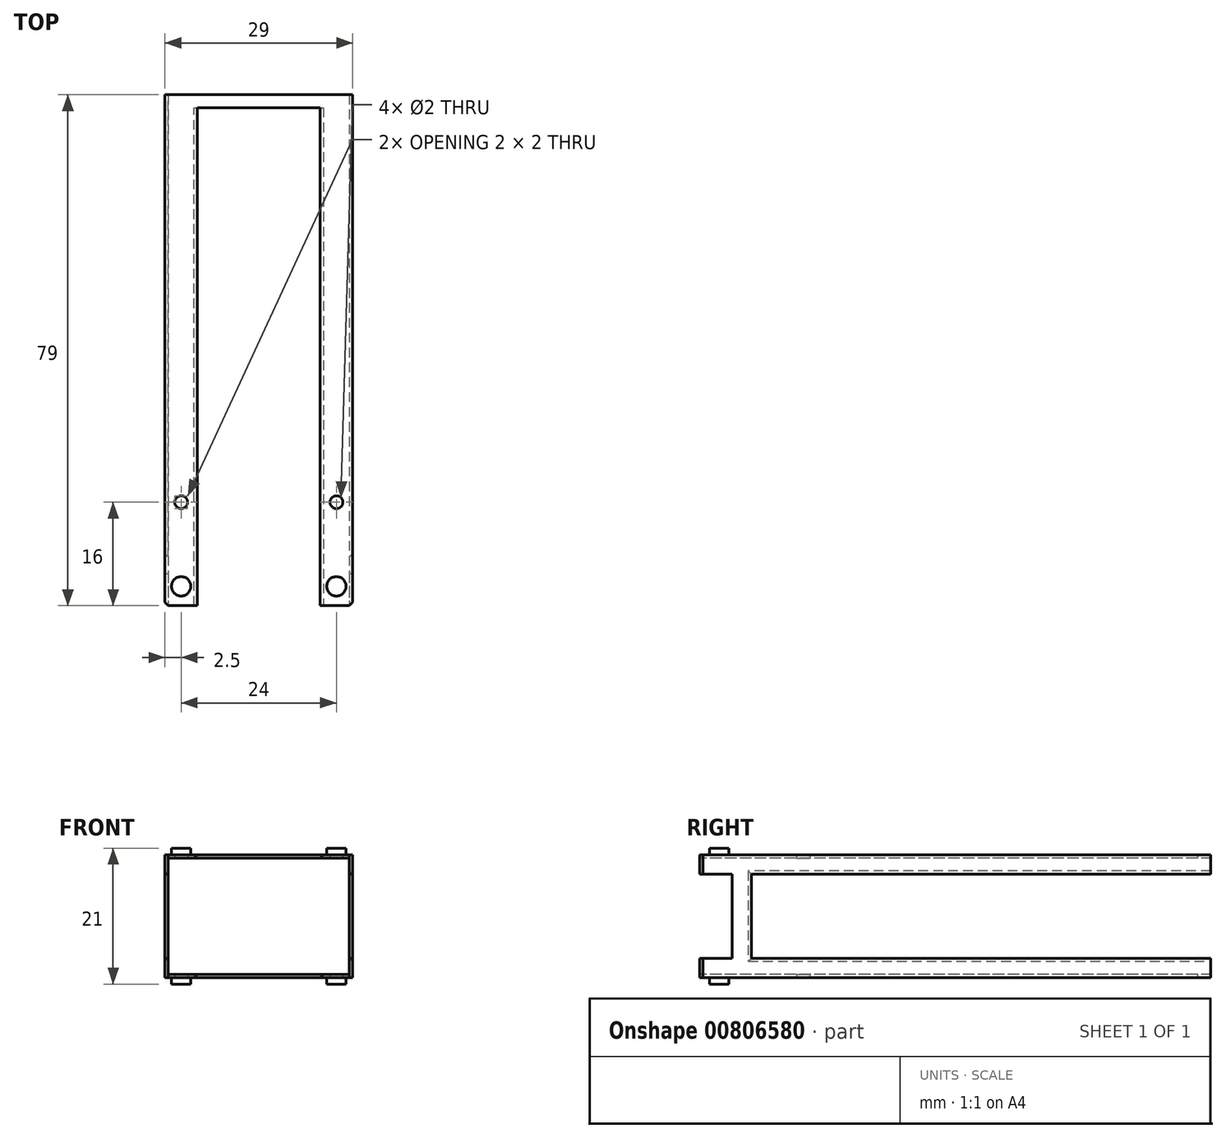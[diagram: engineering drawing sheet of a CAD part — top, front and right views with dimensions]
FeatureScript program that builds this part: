
annotation { "Feature Type Name" : "Feature", "Feature Type Description" : "" }
export const myFeature = defineFeature(function(context is Context, id is Id, definition is map)
    precondition{}
    {
        {
            var Q0;
            Q0=qCreatedBy(makeId("Top.planeOp"),FACE);
            var sketch = newSketch(context, id + "F0", { "sketchPlane" : qUnion([Q0])});
            skLineSegment(sketch, "E0.bottom", {"start": v(-14.5, 79) * mm, "end": v(14.5, 79) * mm});
            skLineSegment(sketch, "E0.top", {"start": v(-14.5, 0) * mm, "end": v(14.5, 0) * mm});
            skLineSegment(sketch, "E0.left", {"start": v(-14.5, 79) * mm, "end": v(-14.5, 0) * mm});
            skLineSegment(sketch, "E0.right", {"start": v(14.5, 79) * mm, "end": v(14.5, 0) * mm});
            skCircle(sketch, "E1", {"center": v(-12, 16) * mm, "radius": 1 * mm});
            skCircle(sketch, "E2", {"center": v(12, 16) * mm, "radius": 1 * mm});
            skCircle(sketch, "E3", {"center": v(-12, 3) * mm, "radius": 1.5 * mm});
            skCircle(sketch, "E4", {"center": v(12, 3) * mm, "radius": 1.5 * mm});
            skSolve(sketch);
        }
        {
            var Q0;
            Q0=makeQuery(id+"F0.imprint","IMPRINT",FACE,{"disambiguationData":[TD([[makeQuery(id+"F0.imprint","IMPRINT",EDGE,{"derivedFrom":sQuery(id+"F0.wireOp",EDGE,"E0.bottom")}),-1.0]])]});
            extrude(context, id + "F1", {"entities" : qUnion([Q0]), "endBound" : BoundingType.SYMMETRIC, "depth" : 19 * mm, "offsetDistance" : 25 * mm});
        }
        {
            var Q0;
            Q0=makeQuery(id+"F0.imprint","IMPRINT",FACE,{"disambiguationData":[TD([[makeQuery(id+"F0.imprint","IMPRINT",EDGE,{"derivedFrom":sQuery(id+"F0.wireOp",EDGE,"E3")}),1.0]])]});
            var Q1;
            Q1=makeQuery(id+"F0.imprint","IMPRINT",FACE,{"disambiguationData":[TD([[makeQuery(id+"F0.imprint","IMPRINT",EDGE,{"derivedFrom":sQuery(id+"F0.wireOp",EDGE,"E4")}),1.0]])]});
            extrude(context, id + "F2", {"entities" : qUnion([Q0, Q1]), "operationType" : NewBodyOperationType.ADD, "endBound" : BoundingType.SYMMETRIC, "depth" : 21 * mm, "offsetDistance" : 25 * mm});
        }
        {
            var Q0;
            Q0=qCreatedBy(makeId("Front.planeOp"),FACE);
            var sketch = newSketch(context, id + "F3", { "sketchPlane" : qUnion([Q0])});
            skLineSegment(sketch, "E5.bottom", {"start": v(-14.5, 9.5) * mm, "end": v(14.5, 9.5) * mm});
            skLineSegment(sketch, "E5.top", {"start": v(-14.5, -9.5) * mm, "end": v(14.5, -9.5) * mm});
            skLineSegment(sketch, "E5.left", {"start": v(-14.5, 9.5) * mm, "end": v(-14.5, -9.5) * mm});
            skLineSegment(sketch, "E5.right", {"start": v(14.5, 9.5) * mm, "end": v(14.5, -9.5) * mm});
            skLineSegment(sketch, "E6.0", {"start": v(-14, 9) * mm, "end": v(14, 9) * mm});
            skLineSegment(sketch, "E6.1", {"start": v(-14, 9) * mm, "end": v(-14, -9) * mm});
            skLineSegment(sketch, "E6.2", {"start": v(-14, -9) * mm, "end": v(14, -9) * mm});
            skLineSegment(sketch, "E6.3", {"start": v(14, 9) * mm, "end": v(14, -9) * mm});
            skLineSegment(sketch, "E7", {"start": v(-14.5, 6.5) * mm, "end": v(-14, 6.5) * mm});
            skLineSegment(sketch, "E8", {"start": v(-14.5, -6.5) * mm, "end": v(-14, -6.5) * mm});
            skLineSegment(sketch, "E9", {"start": v(-9.5, -9) * mm, "end": v(-9.5, -9.5) * mm});
            skLineSegment(sketch, "E10", {"start": v(9.5, -9) * mm, "end": v(9.5, -9.5) * mm});
            skLineSegment(sketch, "E11", {"start": v(14, -6.5) * mm, "end": v(14.5, -6.5) * mm});
            skLineSegment(sketch, "E12", {"start": v(14, 6.5) * mm, "end": v(14.5, 6.5) * mm});
            skLineSegment(sketch, "E13", {"start": v(9.5, 9) * mm, "end": v(9.5, 9.5) * mm});
            skLineSegment(sketch, "E14", {"start": v(-9.5, 9) * mm, "end": v(-9.5, 9.5) * mm});
            skSolve(sketch);
        }
        {
            var Q0;
            {var subQ1=sQuery(id+"F3.wireOp",EDGE,"E6.0");var subQ8=sQuery(id+"F3.wireOp",EDGE,"E6.1");var subQ12=makeQuery(id+"F3.imprint","INTERSECT",VERTEX,{"derivedFrom":[subQ1,subQ8]});Q0=makeQuery(id+"F3.imprint","IMPRINT",FACE,{"disambiguationData":[TD([[makeQuery(id+"F3.imprint","IMPRINT",EDGE,{"disambiguationData":[TD([[subQ12,-1.0]])],"derivedFrom":subQ1}),-1.0]])]});}
            var Q1;
            {var subQ0=sQuery(id+"F3.wireOp",EDGE,"E7");Q1=makeQuery(id+"F3.imprint","IMPRINT",FACE,{"disambiguationData":[TD([[makeQuery(id+"F3.imprint","IMPRINT",EDGE,{"derivedFrom":subQ0}),-1.0]])]});}
            var Q2;
            {var subQ0=sQuery(id+"F3.wireOp",EDGE,"E13");Q2=makeQuery(id+"F3.imprint","IMPRINT",FACE,{"disambiguationData":[TD([[makeQuery(id+"F3.imprint","IMPRINT",EDGE,{"derivedFrom":subQ0}),1.0]])]});}
            var Q3;
            {var subQ0=sQuery(id+"F3.wireOp",EDGE,"E11");Q3=makeQuery(id+"F3.imprint","IMPRINT",FACE,{"disambiguationData":[TD([[makeQuery(id+"F3.imprint","IMPRINT",EDGE,{"derivedFrom":subQ0}),1.0]])]});}
            var Q4;
            {var subQ0=sQuery(id+"F3.wireOp",EDGE,"E9");Q4=makeQuery(id+"F3.imprint","IMPRINT",FACE,{"disambiguationData":[TD([[makeQuery(id+"F3.imprint","IMPRINT",EDGE,{"derivedFrom":subQ0}),1.0]])]});}
            extrude(context, id + "F4", {"entities" : qUnion([Q0, Q1, Q2, Q3, Q4]), "operationType" : NewBodyOperationType.REMOVE, "oppositeDirection" : true, "depth" : 77 * mm, "offsetDistance" : 25 * mm});
        }
        {
            var Q0;
            {var subQ1=sQuery(id+"F3.wireOp",EDGE,"E6.0");var subQ8=sQuery(id+"F3.wireOp",EDGE,"E6.1");var subQ12=makeQuery(id+"F3.imprint","INTERSECT",VERTEX,{"derivedFrom":[subQ1,subQ8]});Q0=makeQuery(id+"F3.imprint","IMPRINT",FACE,{"disambiguationData":[TD([[makeQuery(id+"F3.imprint","IMPRINT",EDGE,{"disambiguationData":[TD([[subQ12,-1.0]])],"derivedFrom":subQ1}),-1.0]])]});}
            var Q1;
            {var subQ0=sQuery(id+"F3.wireOp",EDGE,"E7");Q1=makeQuery(id+"F3.imprint","IMPRINT",FACE,{"disambiguationData":[TD([[makeQuery(id+"F3.imprint","IMPRINT",EDGE,{"derivedFrom":subQ0}),-1.0]])]});}
            var Q2;
            {var subQ0=sQuery(id+"F3.wireOp",EDGE,"E11");Q2=makeQuery(id+"F3.imprint","IMPRINT",FACE,{"disambiguationData":[TD([[makeQuery(id+"F3.imprint","IMPRINT",EDGE,{"derivedFrom":subQ0}),1.0]])]});}
            extrude(context, id + "F5", {"entities" : qUnion([Q0, Q1, Q2]), "operationType" : NewBodyOperationType.REMOVE, "oppositeDirection" : true, "depth" : 79 * mm, "offsetDistance" : 25 * mm});
        }
        {
            var Q0;
            {var subQ0=sQuery(id+"F3.wireOp",EDGE,"E7");Q0=makeQuery(id+"F3.imprint","IMPRINT",FACE,{"disambiguationData":[TD([[makeQuery(id+"F3.imprint","IMPRINT",EDGE,{"derivedFrom":subQ0}),-1.0]])]});}
            var Q1;
            {var subQ0=sQuery(id+"F3.wireOp",EDGE,"E11");Q1=makeQuery(id+"F3.imprint","IMPRINT",FACE,{"disambiguationData":[TD([[makeQuery(id+"F3.imprint","IMPRINT",EDGE,{"derivedFrom":subQ0}),1.0]])]});}
            extrude(context, id + "F6", {"entities" : qUnion([Q0, Q1]), "operationType" : NewBodyOperationType.ADD, "oppositeDirection" : true, "depth" : 8 * mm, "offsetDistance" : 25 * mm});
        }
        {
            var Q0;
            {var subQ0=sQuery(id+"F3.wireOp",EDGE,"E7");Q0=makeQuery(id+"F3.imprint","IMPRINT",FACE,{"disambiguationData":[TD([[makeQuery(id+"F3.imprint","IMPRINT",EDGE,{"derivedFrom":subQ0}),-1.0]])]});}
            var Q1;
            {var subQ0=sQuery(id+"F3.wireOp",EDGE,"E11");Q1=makeQuery(id+"F3.imprint","IMPRINT",FACE,{"disambiguationData":[TD([[makeQuery(id+"F3.imprint","IMPRINT",EDGE,{"derivedFrom":subQ0}),1.0]])]});}
            extrude(context, id + "F7", {"entities" : qUnion([Q0, Q1]), "operationType" : NewBodyOperationType.REMOVE, "oppositeDirection" : true, "depth" : 5 * mm, "offsetDistance" : 25 * mm});
        }
        {
            var Q0;
            Q0=makeQuery(id+"F4.boolean.opBoolean","COPY",EDGE,{"derivedFrom":makeQuery(id+"F4.opExtrude","SWEPT_EDGE",EDGE,{"disambiguationData":[OSD([sQuery(id+"F3.wireOp",EDGE,"E6.2"),sQuery(id+"F3.wireOp",EDGE,"E9")])]})});
            var Q1;
            Q1=makeQuery(id+"F4.boolean.opBoolean","COPY",EDGE,{"derivedFrom":makeQuery(id+"F4.opExtrude","SWEPT_EDGE",EDGE,{"disambiguationData":[OSD([sQuery(id+"F3.wireOp",EDGE,"E6.2"),sQuery(id+"F3.wireOp",EDGE,"E10")])]})});
            var Q2;
            Q2=makeQuery(id+"F4.boolean.opBoolean","COPY",EDGE,{"derivedFrom":makeQuery(id+"F4.opExtrude","SWEPT_EDGE",EDGE,{"disambiguationData":[OSD([sQuery(id+"F3.wireOp",EDGE,"E6.3"),sQuery(id+"F3.wireOp",EDGE,"E11")])]})});
            var Q3;
            Q3=makeQuery(id+"F4.boolean.opBoolean","COPY",EDGE,{"derivedFrom":makeQuery(id+"F4.opExtrude","SWEPT_EDGE",EDGE,{"disambiguationData":[OSD([sQuery(id+"F3.wireOp",EDGE,"E6.1"),sQuery(id+"F3.wireOp",EDGE,"E8")])]})});
            var Q4;
            Q4=makeQuery(id+"F4.boolean.opBoolean","COPY",EDGE,{"derivedFrom":makeQuery(id+"F4.opExtrude","SWEPT_EDGE",EDGE,{"disambiguationData":[OSD([sQuery(id+"F3.wireOp",EDGE,"E6.3"),sQuery(id+"F3.wireOp",EDGE,"E12")])]})});
            var Q5;
            Q5=makeQuery(id+"F4.boolean.opBoolean","COPY",EDGE,{"derivedFrom":makeQuery(id+"F4.opExtrude","SWEPT_EDGE",EDGE,{"disambiguationData":[OSD([sQuery(id+"F3.wireOp",EDGE,"E6.0"),sQuery(id+"F3.wireOp",EDGE,"E13")])]})});
            var Q6;
            Q6=makeQuery(id+"F4.boolean.opBoolean","COPY",EDGE,{"derivedFrom":makeQuery(id+"F4.opExtrude","SWEPT_EDGE",EDGE,{"disambiguationData":[OSD([sQuery(id+"F3.wireOp",EDGE,"E6.1"),sQuery(id+"F3.wireOp",EDGE,"E7")])]})});
            var Q7;
            Q7=makeQuery(id+"F4.boolean.opBoolean","COPY",EDGE,{"derivedFrom":makeQuery(id+"F4.opExtrude","SWEPT_EDGE",EDGE,{"disambiguationData":[OSD([sQuery(id+"F3.wireOp",EDGE,"E6.0"),sQuery(id+"F3.wireOp",EDGE,"E14")])]})});
            var Q8;
            {var subQ0=sQuery(id+"F3.wireOp",EDGE,"E6.3");Q8=makeQuery(id+"F5.boolean.opBoolean","INTERSECT",EDGE,{"derivedFrom":[makeQuery(id+"F4.boolean.opBoolean","COPY",FACE,{"derivedFrom":makeQuery(id+"F4.opExtrude","CAP_FACE",FACE,{"disambiguationData":[OSD([sQuery(id+"F3.wireOp",EDGE,"E5.bottom"),sQuery(id+"F3.wireOp",EDGE,"E5.top"),sQuery(id+"F3.wireOp",EDGE,"E5.left"),sQuery(id+"F3.wireOp",EDGE,"E5.right"),sQuery(id+"F3.wireOp",EDGE,"E6.0"),sQuery(id+"F3.wireOp",EDGE,"E6.1"),sQuery(id+"F3.wireOp",EDGE,"E6.2"),subQ0,sQuery(id+"F3.wireOp",EDGE,"E7"),sQuery(id+"F3.wireOp",EDGE,"E8"),sQuery(id+"F3.wireOp",EDGE,"E9"),sQuery(id+"F3.wireOp",EDGE,"E10"),sQuery(id+"F3.wireOp",EDGE,"E11"),sQuery(id+"F3.wireOp",EDGE,"E12"),sQuery(id+"F3.wireOp",EDGE,"E13"),sQuery(id+"F3.wireOp",EDGE,"E14")])],"isStart":false})}),makeQuery(id+"F5.opExtrude","SWEPT_FACE",FACE,{"disambiguationData":[OSD([subQ0])]})]});}
            var Q9;
            {var subQ0=sQuery(id+"F3.wireOp",EDGE,"E6.1");Q9=makeQuery(id+"F5.boolean.opBoolean","INTERSECT",EDGE,{"derivedFrom":[makeQuery(id+"F4.boolean.opBoolean","COPY",FACE,{"derivedFrom":makeQuery(id+"F4.opExtrude","CAP_FACE",FACE,{"disambiguationData":[OSD([sQuery(id+"F3.wireOp",EDGE,"E5.bottom"),sQuery(id+"F3.wireOp",EDGE,"E5.top"),sQuery(id+"F3.wireOp",EDGE,"E5.left"),sQuery(id+"F3.wireOp",EDGE,"E5.right"),sQuery(id+"F3.wireOp",EDGE,"E6.0"),subQ0,sQuery(id+"F3.wireOp",EDGE,"E6.2"),sQuery(id+"F3.wireOp",EDGE,"E6.3"),sQuery(id+"F3.wireOp",EDGE,"E7"),sQuery(id+"F3.wireOp",EDGE,"E8"),sQuery(id+"F3.wireOp",EDGE,"E9"),sQuery(id+"F3.wireOp",EDGE,"E10"),sQuery(id+"F3.wireOp",EDGE,"E11"),sQuery(id+"F3.wireOp",EDGE,"E12"),sQuery(id+"F3.wireOp",EDGE,"E13"),sQuery(id+"F3.wireOp",EDGE,"E14")])],"isStart":false})}),makeQuery(id+"F5.opExtrude","SWEPT_FACE",FACE,{"disambiguationData":[OSD([subQ0])]})]});}
            var Q10;
            Q10=makeQuery(id+"F7.boolean.opBoolean","COPY",EDGE,{"derivedFrom":makeQuery(id+"F7.opExtrude","CAP_EDGE",EDGE,{"disambiguationData":[OSD([sQuery(id+"F3.wireOp",EDGE,"E6.0")])],"isStart":false})});
            var Q11;
            {var subQ0=sQuery(id+"F0.wireOp",EDGE,"E0.right");var subQ1=makeQuery(id+"F1.opExtrude","SWEPT_FACE",FACE,{"disambiguationData":[OSD([subQ0])]});var subQ3=sQuery(id+"F0.wireOp",EDGE,"E0.top");var subQ6=sQuery(id+"F3.wireOp",EDGE,"E5.bottom");var subQ7=sQuery(id+"F0.wireOp",EDGE,"E0.left");var subQ10=makeQuery(id+"F1.opExtrude","CAP_EDGE",EDGE,{"disambiguationData":[OSD([subQ3])],"isStart":false});Q11=makeQuery(id+"F7.boolean.opBoolean","SPLIT",EDGE,{"disambiguationData":[TD([subQ1])],"derivedFrom":makeQuery(id+"F6.boolean.opBoolean","MERGE",EDGE,{"derivedFrom":[makeQuery(id+"F4.boolean.opBoolean","SPLIT",EDGE,{"disambiguationData":[TD([makeQuery(id+"F1.opExtrude","SWEPT_FACE",FACE,{"disambiguationData":[OSD([subQ7])]})])],"derivedFrom":subQ10}),makeQuery(id+"F4.boolean.opBoolean","SPLIT",EDGE,{"disambiguationData":[TD([subQ1])],"derivedFrom":subQ10}),makeQuery(id+"F6.opExtrude","CAP_EDGE",EDGE,{"disambiguationData":[OSD([subQ6])],"isStart":true})]})});}
            var Q12;
            {var subQ0=sQuery(id+"F0.wireOp",EDGE,"E0.right");var subQ2=sQuery(id+"F3.wireOp",EDGE,"E12");var subQ3=sQuery(id+"F3.wireOp",EDGE,"E11");var subQ4=sQuery(id+"F3.wireOp",EDGE,"E5.right");var subQ5=sQuery(id+"F0.wireOp",EDGE,"E0.top");var subQ12=sQuery(id+"F3.wireOp",EDGE,"E5.top");var subQ13=makeQuery(id+"F1.opExtrude","SWEPT_EDGE",EDGE,{"disambiguationData":[OSD([subQ5,subQ0])]});Q12=makeQuery(id+"F7.boolean.opBoolean","SPLIT",EDGE,{"disambiguationData":[TD([makeQuery(id+"F6.opExtrude","SWEPT_FACE",FACE,{"disambiguationData":[OSD([subQ12])]})])],"derivedFrom":makeQuery(id+"F6.boolean.opBoolean","MERGE",EDGE,{"derivedFrom":[makeQuery(id+"F4.boolean.opBoolean","SPLIT",EDGE,{"disambiguationData":[TD([makeQuery(id+"F4.opExtrude","SWEPT_FACE",FACE,{"disambiguationData":[OSD([subQ3])]})])],"derivedFrom":subQ13}),makeQuery(id+"F4.boolean.opBoolean","SPLIT",EDGE,{"disambiguationData":[TD([makeQuery(id+"F4.opExtrude","SWEPT_FACE",FACE,{"disambiguationData":[OSD([subQ2])]})])],"derivedFrom":subQ13}),makeQuery(id+"F6.opExtrude","CAP_EDGE",EDGE,{"disambiguationData":[OSD([subQ4])],"isStart":true})]})});}
            var Q13;
            {var subQ0=sQuery(id+"F0.wireOp",EDGE,"E0.right");var subQ2=sQuery(id+"F3.wireOp",EDGE,"E12");var subQ3=sQuery(id+"F3.wireOp",EDGE,"E11");var subQ4=sQuery(id+"F3.wireOp",EDGE,"E5.right");var subQ5=sQuery(id+"F0.wireOp",EDGE,"E0.top");var subQ7=sQuery(id+"F3.wireOp",EDGE,"E5.bottom");var subQ13=makeQuery(id+"F1.opExtrude","SWEPT_EDGE",EDGE,{"disambiguationData":[OSD([subQ5,subQ0])]});Q13=makeQuery(id+"F7.boolean.opBoolean","SPLIT",EDGE,{"disambiguationData":[TD([makeQuery(id+"F6.opExtrude","SWEPT_FACE",FACE,{"disambiguationData":[OSD([subQ7])]})])],"derivedFrom":makeQuery(id+"F6.boolean.opBoolean","MERGE",EDGE,{"derivedFrom":[makeQuery(id+"F4.boolean.opBoolean","SPLIT",EDGE,{"disambiguationData":[TD([makeQuery(id+"F4.opExtrude","SWEPT_FACE",FACE,{"disambiguationData":[OSD([subQ3])]})])],"derivedFrom":subQ13}),makeQuery(id+"F4.boolean.opBoolean","SPLIT",EDGE,{"disambiguationData":[TD([makeQuery(id+"F4.opExtrude","SWEPT_FACE",FACE,{"disambiguationData":[OSD([subQ2])]})])],"derivedFrom":subQ13}),makeQuery(id+"F6.opExtrude","CAP_EDGE",EDGE,{"disambiguationData":[OSD([subQ4])],"isStart":true})]})});}
            var Q14;
            {var subQ0=sQuery(id+"F0.wireOp",EDGE,"E0.right");var subQ1=makeQuery(id+"F1.opExtrude","SWEPT_FACE",FACE,{"disambiguationData":[OSD([subQ0])]});var subQ3=sQuery(id+"F0.wireOp",EDGE,"E0.top");var subQ5=sQuery(id+"F0.wireOp",EDGE,"E0.left");var subQ7=sQuery(id+"F3.wireOp",EDGE,"E5.top");var subQ10=makeQuery(id+"F1.opExtrude","CAP_EDGE",EDGE,{"disambiguationData":[OSD([subQ3])],"isStart":true});Q14=makeQuery(id+"F7.boolean.opBoolean","SPLIT",EDGE,{"disambiguationData":[TD([subQ1])],"derivedFrom":makeQuery(id+"F6.boolean.opBoolean","MERGE",EDGE,{"derivedFrom":[makeQuery(id+"F4.boolean.opBoolean","SPLIT",EDGE,{"disambiguationData":[TD([makeQuery(id+"F1.opExtrude","SWEPT_FACE",FACE,{"disambiguationData":[OSD([subQ5])]})])],"derivedFrom":subQ10}),makeQuery(id+"F4.boolean.opBoolean","SPLIT",EDGE,{"disambiguationData":[TD([subQ1])],"derivedFrom":subQ10}),makeQuery(id+"F6.opExtrude","CAP_EDGE",EDGE,{"disambiguationData":[OSD([subQ7])],"isStart":true})]})});}
            var Q15;
            {var subQ0=sQuery(id+"F0.wireOp",EDGE,"E0.left");var subQ1=makeQuery(id+"F1.opExtrude","SWEPT_FACE",FACE,{"disambiguationData":[OSD([subQ0])]});var subQ2=sQuery(id+"F0.wireOp",EDGE,"E0.top");var subQ4=sQuery(id+"F0.wireOp",EDGE,"E0.right");var subQ7=sQuery(id+"F3.wireOp",EDGE,"E5.top");var subQ10=makeQuery(id+"F1.opExtrude","CAP_EDGE",EDGE,{"disambiguationData":[OSD([subQ2])],"isStart":true});Q15=makeQuery(id+"F7.boolean.opBoolean","SPLIT",EDGE,{"disambiguationData":[TD([subQ1])],"derivedFrom":makeQuery(id+"F6.boolean.opBoolean","MERGE",EDGE,{"derivedFrom":[makeQuery(id+"F4.boolean.opBoolean","SPLIT",EDGE,{"disambiguationData":[TD([subQ1])],"derivedFrom":subQ10}),makeQuery(id+"F4.boolean.opBoolean","SPLIT",EDGE,{"disambiguationData":[TD([makeQuery(id+"F1.opExtrude","SWEPT_FACE",FACE,{"disambiguationData":[OSD([subQ4])]})])],"derivedFrom":subQ10}),makeQuery(id+"F6.opExtrude","CAP_EDGE",EDGE,{"disambiguationData":[OSD([subQ7])],"isStart":true})]})});}
            var Q16;
            Q16=makeQuery(id+"F7.boolean.opBoolean","COPY",EDGE,{"derivedFrom":makeQuery(id+"F7.opExtrude","CAP_EDGE",EDGE,{"disambiguationData":[OSD([sQuery(id+"F3.wireOp",EDGE,"E6.2")])],"isStart":false})});
            var Q17;
            {var subQ0=sQuery(id+"F0.wireOp",EDGE,"E0.left");var subQ2=sQuery(id+"F0.wireOp",EDGE,"E0.top");var subQ9=sQuery(id+"F3.wireOp",EDGE,"E5.left");var subQ10=sQuery(id+"F3.wireOp",EDGE,"E5.top");var subQ11=sQuery(id+"F3.wireOp",EDGE,"E8");var subQ12=sQuery(id+"F3.wireOp",EDGE,"E7");var subQ13=makeQuery(id+"F1.opExtrude","SWEPT_EDGE",EDGE,{"disambiguationData":[OSD([subQ2,subQ0])]});Q17=makeQuery(id+"F7.boolean.opBoolean","SPLIT",EDGE,{"disambiguationData":[TD([makeQuery(id+"F6.opExtrude","SWEPT_FACE",FACE,{"disambiguationData":[OSD([subQ10])]})])],"derivedFrom":makeQuery(id+"F6.boolean.opBoolean","MERGE",EDGE,{"derivedFrom":[makeQuery(id+"F4.boolean.opBoolean","SPLIT",EDGE,{"disambiguationData":[TD([makeQuery(id+"F4.opExtrude","SWEPT_FACE",FACE,{"disambiguationData":[OSD([subQ11])]})])],"derivedFrom":subQ13}),makeQuery(id+"F4.boolean.opBoolean","SPLIT",EDGE,{"disambiguationData":[TD([makeQuery(id+"F4.opExtrude","SWEPT_FACE",FACE,{"disambiguationData":[OSD([subQ12])]})])],"derivedFrom":subQ13}),makeQuery(id+"F6.opExtrude","CAP_EDGE",EDGE,{"disambiguationData":[OSD([subQ9])],"isStart":true})]})});}
            var Q18;
            {var subQ0=sQuery(id+"F0.wireOp",EDGE,"E0.left");var subQ2=sQuery(id+"F0.wireOp",EDGE,"E0.top");var subQ4=sQuery(id+"F3.wireOp",EDGE,"E5.bottom");var subQ10=sQuery(id+"F3.wireOp",EDGE,"E8");var subQ11=sQuery(id+"F3.wireOp",EDGE,"E7");var subQ12=sQuery(id+"F3.wireOp",EDGE,"E5.left");var subQ13=makeQuery(id+"F1.opExtrude","SWEPT_EDGE",EDGE,{"disambiguationData":[OSD([subQ2,subQ0])]});Q18=makeQuery(id+"F7.boolean.opBoolean","SPLIT",EDGE,{"disambiguationData":[TD([makeQuery(id+"F6.opExtrude","SWEPT_FACE",FACE,{"disambiguationData":[OSD([subQ4])]})])],"derivedFrom":makeQuery(id+"F6.boolean.opBoolean","MERGE",EDGE,{"derivedFrom":[makeQuery(id+"F4.boolean.opBoolean","SPLIT",EDGE,{"disambiguationData":[TD([makeQuery(id+"F4.opExtrude","SWEPT_FACE",FACE,{"disambiguationData":[OSD([subQ10])]})])],"derivedFrom":subQ13}),makeQuery(id+"F4.boolean.opBoolean","SPLIT",EDGE,{"disambiguationData":[TD([makeQuery(id+"F4.opExtrude","SWEPT_FACE",FACE,{"disambiguationData":[OSD([subQ11])]})])],"derivedFrom":subQ13}),makeQuery(id+"F6.opExtrude","CAP_EDGE",EDGE,{"disambiguationData":[OSD([subQ12])],"isStart":true})]})});}
            var Q19;
            {var subQ0=sQuery(id+"F0.wireOp",EDGE,"E0.left");var subQ1=makeQuery(id+"F1.opExtrude","SWEPT_FACE",FACE,{"disambiguationData":[OSD([subQ0])]});var subQ3=sQuery(id+"F0.wireOp",EDGE,"E0.top");var subQ5=sQuery(id+"F3.wireOp",EDGE,"E5.bottom");var subQ6=sQuery(id+"F0.wireOp",EDGE,"E0.right");var subQ10=makeQuery(id+"F1.opExtrude","CAP_EDGE",EDGE,{"disambiguationData":[OSD([subQ3])],"isStart":false});Q19=makeQuery(id+"F7.boolean.opBoolean","SPLIT",EDGE,{"disambiguationData":[TD([subQ1])],"derivedFrom":makeQuery(id+"F6.boolean.opBoolean","MERGE",EDGE,{"derivedFrom":[makeQuery(id+"F4.boolean.opBoolean","SPLIT",EDGE,{"disambiguationData":[TD([subQ1])],"derivedFrom":subQ10}),makeQuery(id+"F4.boolean.opBoolean","SPLIT",EDGE,{"disambiguationData":[TD([makeQuery(id+"F1.opExtrude","SWEPT_FACE",FACE,{"disambiguationData":[OSD([subQ6])]})])],"derivedFrom":subQ10}),makeQuery(id+"F6.opExtrude","CAP_EDGE",EDGE,{"disambiguationData":[OSD([subQ5])],"isStart":true})]})});}
            var Q20;
            Q20=makeQuery(id+"F7.boolean.opBoolean","COPY",EDGE,{"derivedFrom":makeQuery(id+"F7.opExtrude","CAP_EDGE",EDGE,{"disambiguationData":[OSD([sQuery(id+"F3.wireOp",EDGE,"E6.1")])],"isStart":false})});
            var Q21;
            Q21=makeQuery(id+"F7.boolean.opBoolean","COPY",EDGE,{"derivedFrom":makeQuery(id+"F7.opExtrude","CAP_EDGE",EDGE,{"disambiguationData":[OSD([sQuery(id+"F3.wireOp",EDGE,"E6.3")])],"isStart":false})});
            var Q22;
            Q22=makeQuery(id+"F6.opExtrude","CAP_EDGE",EDGE,{"disambiguationData":[OSD([sQuery(id+"F3.wireOp",EDGE,"E6.1")])],"isStart":false});
            var Q23;
            Q23=makeQuery(id+"F6.opExtrude","CAP_EDGE",EDGE,{"disambiguationData":[OSD([sQuery(id+"F3.wireOp",EDGE,"E6.3")])],"isStart":false});
            var Q24;
            {var subQ0=sQuery(id+"F3.wireOp",EDGE,"E5.left");var subQ1=sQuery(id+"F0.wireOp",EDGE,"E0.left");var subQ3=sQuery(id+"F0.wireOp",EDGE,"E0.top");var subQ12=sQuery(id+"F3.wireOp",EDGE,"E8");var subQ13=sQuery(id+"F3.wireOp",EDGE,"E7");var subQ14=makeQuery(id+"F1.opExtrude","SWEPT_EDGE",EDGE,{"disambiguationData":[OSD([subQ3,subQ1])]});Q24=makeQuery(id+"F7.boolean.opBoolean","SPLIT",EDGE,{"disambiguationData":[TD([makeQuery(id+"F7.opExtrude","SWEPT_FACE",FACE,{"disambiguationData":[OSD([subQ12])]})])],"derivedFrom":makeQuery(id+"F6.boolean.opBoolean","MERGE",EDGE,{"derivedFrom":[makeQuery(id+"F4.boolean.opBoolean","SPLIT",EDGE,{"disambiguationData":[TD([makeQuery(id+"F4.opExtrude","SWEPT_FACE",FACE,{"disambiguationData":[OSD([subQ12])]})])],"derivedFrom":subQ14}),makeQuery(id+"F4.boolean.opBoolean","SPLIT",EDGE,{"disambiguationData":[TD([makeQuery(id+"F4.opExtrude","SWEPT_FACE",FACE,{"disambiguationData":[OSD([subQ13])]})])],"derivedFrom":subQ14}),makeQuery(id+"F6.opExtrude","CAP_EDGE",EDGE,{"disambiguationData":[OSD([subQ0])],"isStart":true})]})});}
            var Q25;
            {var subQ0=sQuery(id+"F3.wireOp",EDGE,"E5.right");var subQ1=sQuery(id+"F0.wireOp",EDGE,"E0.right");var subQ3=sQuery(id+"F0.wireOp",EDGE,"E0.top");var subQ12=sQuery(id+"F3.wireOp",EDGE,"E12");var subQ13=sQuery(id+"F3.wireOp",EDGE,"E11");var subQ14=makeQuery(id+"F1.opExtrude","SWEPT_EDGE",EDGE,{"disambiguationData":[OSD([subQ3,subQ1])]});Q25=makeQuery(id+"F7.boolean.opBoolean","SPLIT",EDGE,{"disambiguationData":[TD([makeQuery(id+"F7.opExtrude","SWEPT_FACE",FACE,{"disambiguationData":[OSD([subQ13])]})])],"derivedFrom":makeQuery(id+"F6.boolean.opBoolean","MERGE",EDGE,{"derivedFrom":[makeQuery(id+"F4.boolean.opBoolean","SPLIT",EDGE,{"disambiguationData":[TD([makeQuery(id+"F4.opExtrude","SWEPT_FACE",FACE,{"disambiguationData":[OSD([subQ13])]})])],"derivedFrom":subQ14}),makeQuery(id+"F4.boolean.opBoolean","SPLIT",EDGE,{"disambiguationData":[TD([makeQuery(id+"F4.opExtrude","SWEPT_FACE",FACE,{"disambiguationData":[OSD([subQ12])]})])],"derivedFrom":subQ14}),makeQuery(id+"F6.opExtrude","CAP_EDGE",EDGE,{"disambiguationData":[OSD([subQ0])],"isStart":true})]})});}
            var Q26;
            {var subQ0=sQuery(id+"F3.wireOp",EDGE,"E5.right");var subQ1=sQuery(id+"F0.wireOp",EDGE,"E0.right");var subQ3=sQuery(id+"F0.wireOp",EDGE,"E0.top");var subQ5=sQuery(id+"F3.wireOp",EDGE,"E12");var subQ13=sQuery(id+"F3.wireOp",EDGE,"E11");var subQ14=makeQuery(id+"F1.opExtrude","SWEPT_EDGE",EDGE,{"disambiguationData":[OSD([subQ3,subQ1])]});Q26=makeQuery(id+"F7.boolean.opBoolean","SPLIT",EDGE,{"disambiguationData":[TD([makeQuery(id+"F7.opExtrude","SWEPT_FACE",FACE,{"disambiguationData":[OSD([subQ5])]})])],"derivedFrom":makeQuery(id+"F6.boolean.opBoolean","MERGE",EDGE,{"derivedFrom":[makeQuery(id+"F4.boolean.opBoolean","SPLIT",EDGE,{"disambiguationData":[TD([makeQuery(id+"F4.opExtrude","SWEPT_FACE",FACE,{"disambiguationData":[OSD([subQ13])]})])],"derivedFrom":subQ14}),makeQuery(id+"F4.boolean.opBoolean","SPLIT",EDGE,{"disambiguationData":[TD([makeQuery(id+"F4.opExtrude","SWEPT_FACE",FACE,{"disambiguationData":[OSD([subQ5])]})])],"derivedFrom":subQ14}),makeQuery(id+"F6.opExtrude","CAP_EDGE",EDGE,{"disambiguationData":[OSD([subQ0])],"isStart":true})]})});}
            var Q27;
            {var subQ0=sQuery(id+"F0.wireOp",EDGE,"E0.left");var subQ2=sQuery(id+"F0.wireOp",EDGE,"E0.top");var subQ4=sQuery(id+"F3.wireOp",EDGE,"E5.left");var subQ12=sQuery(id+"F3.wireOp",EDGE,"E8");var subQ13=sQuery(id+"F3.wireOp",EDGE,"E7");var subQ14=makeQuery(id+"F1.opExtrude","SWEPT_EDGE",EDGE,{"disambiguationData":[OSD([subQ2,subQ0])]});Q27=makeQuery(id+"F7.boolean.opBoolean","SPLIT",EDGE,{"disambiguationData":[TD([makeQuery(id+"F7.opExtrude","SWEPT_FACE",FACE,{"disambiguationData":[OSD([subQ13])]})])],"derivedFrom":makeQuery(id+"F6.boolean.opBoolean","MERGE",EDGE,{"derivedFrom":[makeQuery(id+"F4.boolean.opBoolean","SPLIT",EDGE,{"disambiguationData":[TD([makeQuery(id+"F4.opExtrude","SWEPT_FACE",FACE,{"disambiguationData":[OSD([subQ12])]})])],"derivedFrom":subQ14}),makeQuery(id+"F4.boolean.opBoolean","SPLIT",EDGE,{"disambiguationData":[TD([makeQuery(id+"F4.opExtrude","SWEPT_FACE",FACE,{"disambiguationData":[OSD([subQ13])]})])],"derivedFrom":subQ14}),makeQuery(id+"F6.opExtrude","CAP_EDGE",EDGE,{"disambiguationData":[OSD([subQ4])],"isStart":true})]})});}
            chamfer(context, id + "F8", {"entities" : qUnion([Q0, Q1, Q2, Q3, Q4, Q5, Q6, Q7, Q8, Q9, Q10, Q11, Q12, Q13, Q14, Q15, Q16, Q17, Q18, Q19, Q20, Q21, Q22, Q23, Q24, Q25, Q26, Q27]), "chamferType" : ChamferType.OFFSET_ANGLE, "width" : 0.5 * mm, "oppositeDirection" : true, "angle" : 45 * degree});
        }
    });
